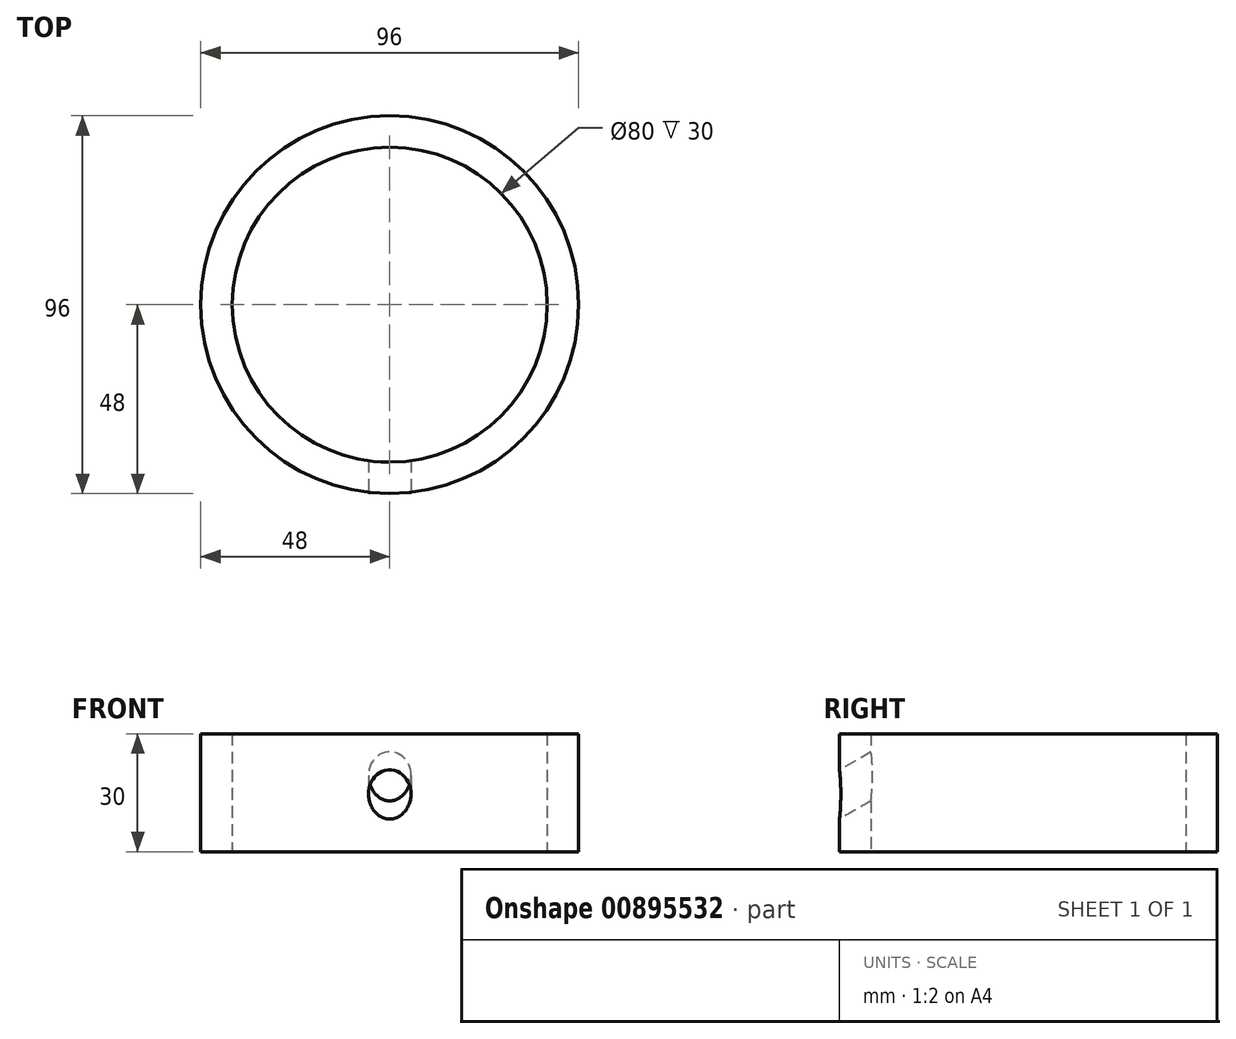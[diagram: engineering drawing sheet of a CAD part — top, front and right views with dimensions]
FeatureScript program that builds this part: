
annotation { "Feature Type Name" : "Feature", "Feature Type Description" : "" }
export const myFeature = defineFeature(function(context is Context, id is Id, definition is map)
    precondition{}
    {
        {
            var Q0;
            Q0=qCreatedBy(makeId("Top.planeOp"),FACE);
            var sketch = newSketch(context, id + "F0", { "sketchPlane" : qUnion([Q0])});
            skCircle(sketch, "E0", {"center": v(0, 0) * mm, "radius": 50 * mm});
            skCircle(sketch, "E1.0", {"center": v(0, 0) * mm, "radius": 48 * mm});
            skCircle(sketch, "E2.0", {"center": v(0, 0) * mm, "radius": 40 * mm});
            skSolve(sketch);
        }
        {
            var Q0;
            {var subQ0=sQuery(id+"F0.wireOp",EDGE,"eVyIfSKI-yzFt-boip-X8GP-brEcGweP3NaP");var subQ1=sQuery(id+"F0.wireOp",EDGE,"E1.0");var subQ2=makeQuery(id+"F0.imprint","INTERSECT",VERTEX,{"derivedFrom":[subQ1,subQ0]});Q0=makeQuery(id+"F0.imprint","IMPRINT",FACE,{"disambiguationData":[TD([[makeQuery(id+"F0.imprint","IMPRINT",EDGE,{"disambiguationData":[TD([[subQ2,-1.0]])],"derivedFrom":subQ1}),1.0]])]});}
            extrude(context, id + "F1", {"entities" : qUnion([Q0]), "depth" : 30 * mm, "offsetDistance" : 25 * mm});
        }
        {
            var Q0;
            Q0=qCreatedBy(makeId("Front.planeOp"),FACE);
            cPlane(context, id + "F2", {"entities" : qUnion([Q0]), "cplaneType" : CPlaneType.OFFSET, "offset" : 48 * mm, "width" : 150 * mm, "height" : 150 * mm});
        }
        {
            var Q0;
            Q0=qCreatedBy(id+"F2.planeOp",FACE);
            var sketch = newSketch(context, id + "F3", { "sketchPlane" : qUnion([Q0])});
            skLineSegment(sketch, "E3", {"start": v(0, 0) * mm, "end": v(0, 30) * mm});
            skSolve(sketch);
        }
        {
            var Q0;
            Q0=sQuery(id+"F3.wireOp",EDGE,"E3");
            cPlane(context, id + "F4", {"entities" : qUnion([Q0]), "cplaneType" : CPlaneType.LINE_ANGLE, "offset" : 25 * mm, "angle" : 0 * degree, "width" : 150 * mm, "height" : 150 * mm});
        }
        {
            var Q0;
            Q0=qCreatedBy(id+"F4.planeOp",FACE);
            var sketch = newSketch(context, id + "F5", { "sketchPlane" : qUnion([Q0])});
            skLineSegment(sketch, "E4", {"start": v(48, 30) * mm, "end": v(48, 0) * mm});
            skLineSegment(sketch, "E5", {"start": v(-48, 0) * mm, "end": v(-48, 30) * mm});
            skLineSegment(sketch, "E6", {"start": v(-48, 0) * mm, "end": v(-65.32, 30) * mm});
            skSolve(sketch);
        }
        {
            var Q0;
            Q0=sQuery(id+"F5.wireOp",EDGE,"E6");
            cPlane(context, id + "F6", {"entities" : qUnion([Q0]), "cplaneType" : CPlaneType.LINE_ANGLE, "offset" : 25 * mm, "angle" : 90 * degree, "width" : 150 * mm, "height" : 150 * mm});
        }
        {
            var Q0;
            Q0=qCreatedBy(id+"F6.planeOp",FACE);
            var sketch = newSketch(context, id + "F7", { "sketchPlane" : qUnion([Q0])});
            skLineSegment(sketch, "E7", {"start": v(-48, 0) * mm, "end": v(-48, 25.98) * mm});
            skLineSegment(sketch, "E8", {"start": v(48, 25.98) * mm, "end": v(48, 0) * mm});
            skLineSegment(sketch, "E9", {"start": v(48, 25.98) * mm, "end": v(-48, 25.98) * mm});
            skLineSegment(sketch, "E10", {"start": v(0, 25.98) * mm, "end": v(0, 68.46) * mm});
            skLineSegment(sketch, "E11", {"start": v(0, 68.46) * mm, "end": v(-48, 25.98) * mm});
            skLineSegment(sketch, "E12", {"start": v(0, 68.46) * mm, "end": v(48, 25.98) * mm});
            skLineSegment(sketch, "E13", {"start": v(0, 25.98) * mm, "end": v(0, 47.22) * mm});
            skLineSegment(sketch, "E14", {"start": v(0, 47.22) * mm, "end": v(-5.29, 47.22) * mm});
            skLineSegment(sketch, "E15", {"start": v(0, 47.22) * mm, "end": v(0, 36.6) * mm});
            skLineSegment(sketch, "E16", {"start": v(0, 36.6) * mm, "end": v(5.4, 36.6) * mm});
            skCircle(sketch, "E17", {"center": v(0, 36.6) * mm, "radius": 5.4 * mm});
            skSolve(sketch);
        }
        {
            var Q0;
            {var subQ1=sQuery(id+"F7.wireOp",EDGE,"E13");var subQ3=sQuery(id+"F7.wireOp",EDGE,"E17");var subQ4=makeQuery(id+"F7.imprint","INTERSECT",VERTEX,{"derivedFrom":[subQ1,subQ3]});Q0=makeQuery(id+"F7.imprint","IMPRINT",FACE,{"disambiguationData":[TD([[makeQuery(id+"F7.imprint","IMPRINT",EDGE,{"disambiguationData":[TD([[subQ4,1.0]])],"derivedFrom":subQ3}),1.0]])]});}
            var Q1;
            {var subQ0=sQuery(id+"F7.wireOp",EDGE,"E16");var subQ3=sQuery(id+"F7.wireOp",EDGE,"E17");var subQ5=makeQuery(id+"F7.imprint","INTERSECT",VERTEX,{"derivedFrom":[subQ0,subQ3]});Q1=makeQuery(id+"F7.imprint","IMPRINT",FACE,{"disambiguationData":[TD([[makeQuery(id+"F7.imprint","IMPRINT",EDGE,{"disambiguationData":[TD([[subQ5,-1.0]])],"derivedFrom":subQ3}),1.0]])]});}
            var Q2;
            {var subQ0=sQuery(id+"F7.wireOp",EDGE,"E16");var subQ3=sQuery(id+"F7.wireOp",EDGE,"E17");var subQ5=makeQuery(id+"F7.imprint","INTERSECT",VERTEX,{"derivedFrom":[subQ0,subQ3]});Q2=makeQuery(id+"F7.imprint","IMPRINT",FACE,{"disambiguationData":[TD([[makeQuery(id+"F7.imprint","IMPRINT",EDGE,{"disambiguationData":[TD([[subQ5,1.0]])],"derivedFrom":subQ3}),1.0]])]});}
            extrude(context, id + "F8", {"entities" : qUnion([Q0, Q1, Q2]), "operationType" : NewBodyOperationType.REMOVE, "depth" : 25 * mm, "offsetDistance" : 25 * mm});
        }
    });
